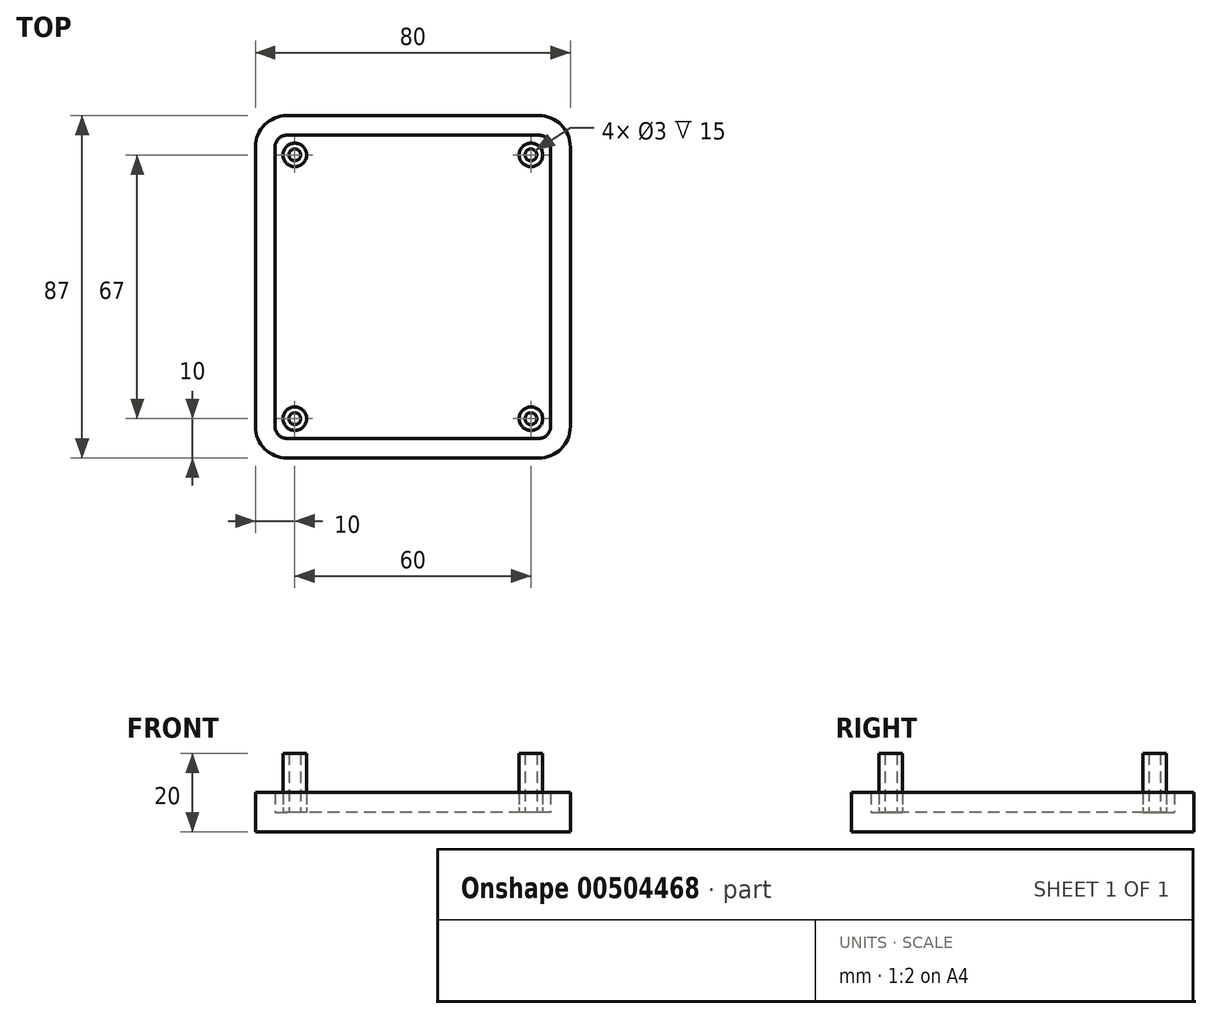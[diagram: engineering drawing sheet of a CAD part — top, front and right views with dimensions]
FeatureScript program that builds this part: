
annotation { "Feature Type Name" : "Feature", "Feature Type Description" : "" }
export const myFeature = defineFeature(function(context is Context, id is Id, definition is map)
    precondition{}
    {
        {
            var Q0;
            Q0=qCreatedBy(makeId("Top.planeOp"),FACE);
            var sketch = newSketch(context, id + "F0", { "sketchPlane" : qUnion([Q0])});
            skLineSegment(sketch, "E0.bottom", {"start": v(32, 38.5) * mm, "end": v(-32, 38.5) * mm});
            skLineSegment(sketch, "E0.top", {"start": v(32, -38.5) * mm, "end": v(-32, -38.5) * mm});
            skLineSegment(sketch, "E0.left", {"start": v(35, 35.5) * mm, "end": v(35, -35.5) * mm});
            skLineSegment(sketch, "E0.right", {"start": v(-35, 35.5) * mm, "end": v(-35, -35.5) * mm});
            skPoint(sketch, "E0.middle", {"position": v(0, 0) * mm});
            skPoint(sketch, "E1.visualSharp", {"position": v(-35, 38.5) * mm});
            skArc(sketch, "E1.filletArc", {"start": v(-32, 38.5) * mm, "mid": v(-34.12, 37.62) * mm, "end": v(-35, 35.5) * mm});
            skPoint(sketch, "E2.visualSharp", {"position": v(35, 38.5) * mm});
            skArc(sketch, "E2.filletArc", {"start": v(35, 35.5) * mm, "mid": v(34.12, 37.62) * mm, "end": v(32, 38.5) * mm});
            skPoint(sketch, "E3.visualSharp", {"position": v(35, -38.5) * mm});
            skArc(sketch, "E3.filletArc", {"start": v(32, -38.5) * mm, "mid": v(34.12, -37.62) * mm, "end": v(35, -35.5) * mm});
            skPoint(sketch, "E4.visualSharp", {"position": v(-35, -38.5) * mm});
            skArc(sketch, "E4.filletArc", {"start": v(-35, -35.5) * mm, "mid": v(-34.12, -37.62) * mm, "end": v(-32, -38.5) * mm});
            skLineSegment(sketch, "E5.bottom", {"start": v(32, 43.5) * mm, "end": v(-32, 43.5) * mm});
            skLineSegment(sketch, "E5.top", {"start": v(32, -43.5) * mm, "end": v(-32, -43.5) * mm});
            skLineSegment(sketch, "E5.left", {"start": v(40, 35.5) * mm, "end": v(40, -35.5) * mm});
            skLineSegment(sketch, "E5.right", {"start": v(-40, 35.5) * mm, "end": v(-40, -35.5) * mm});
            skPoint(sketch, "E6.visualSharp", {"position": v(-40, 43.5) * mm});
            skArc(sketch, "E6.filletArc", {"start": v(-32, 43.5) * mm, "mid": v(-37.66, 41.16) * mm, "end": v(-40, 35.5) * mm});
            skPoint(sketch, "E7.visualSharp", {"position": v(40, 43.5) * mm});
            skArc(sketch, "E7.filletArc", {"start": v(40, 35.5) * mm, "mid": v(37.66, 41.16) * mm, "end": v(32, 43.5) * mm});
            skPoint(sketch, "E8.visualSharp", {"position": v(40, -43.5) * mm});
            skArc(sketch, "E8.filletArc", {"start": v(32, -43.5) * mm, "mid": v(37.66, -41.16) * mm, "end": v(40, -35.5) * mm});
            skPoint(sketch, "E9.visualSharp", {"position": v(-40, -43.5) * mm});
            skArc(sketch, "E9.filletArc", {"start": v(-40, -35.5) * mm, "mid": v(-37.66, -41.16) * mm, "end": v(-32, -43.5) * mm});
            skCircle(sketch, "E10", {"center": v(30, 33.5) * mm, "radius": 2 * mm, "construction": true});
            skCircle(sketch, "E11", {"center": v(-30, 33.5) * mm, "radius": 2 * mm, "construction": true});
            skCircle(sketch, "E12", {"center": v(-30, -33.5) * mm, "radius": 2 * mm, "construction": true});
            skCircle(sketch, "E13", {"center": v(30, -33.5) * mm, "radius": 2 * mm, "construction": true});
            skCircle(sketch, "E14", {"center": v(-30, 33.5) * mm, "radius": 1.5 * mm});
            skCircle(sketch, "E15", {"center": v(-30, 33.5) * mm, "radius": 3 * mm});
            skCircle(sketch, "E16", {"center": v(30, 33.5) * mm, "radius": 1.5 * mm});
            skCircle(sketch, "E17", {"center": v(30, 33.5) * mm, "radius": 3 * mm});
            skCircle(sketch, "E18", {"center": v(30, -33.5) * mm, "radius": 1.5 * mm});
            skCircle(sketch, "E19", {"center": v(30, -33.5) * mm, "radius": 3 * mm});
            skCircle(sketch, "E20", {"center": v(-30, -33.5) * mm, "radius": 1.5 * mm});
            skCircle(sketch, "E21", {"center": v(-30, -33.5) * mm, "radius": 3 * mm});
            skSolve(sketch);
        }
        {
            var Q0;
            Q0=makeQuery(id+"F0.imprint","IMPRINT",FACE,{"disambiguationData":[TD([[makeQuery(id+"F0.imprint","IMPRINT",EDGE,{"derivedFrom":sQuery(id+"F0.wireOp",EDGE,"E0.bottom")}),-1.0]])]});
            extrude(context, id + "F1", {"entities" : qUnion([Q0]), "depth" : 10 * mm});
        }
        {
            var Q0;
            Q0=makeQuery(id+"F0.imprint","IMPRINT",FACE,{"disambiguationData":[TD([[makeQuery(id+"F0.imprint","IMPRINT",EDGE,{"derivedFrom":sQuery(id+"F0.wireOp",EDGE,"E0.bottom")}),1.0]])]});
            var Q1;
            Q1=makeQuery(id+"F0.imprint","IMPRINT",FACE,{"disambiguationData":[TD([[makeQuery(id+"F0.imprint","IMPRINT",EDGE,{"derivedFrom":sQuery(id+"F0.wireOp",EDGE,"E20")}),1.0]])]});
            var Q2;
            Q2=makeQuery(id+"F0.imprint","IMPRINT",FACE,{"disambiguationData":[TD([[makeQuery(id+"F0.imprint","IMPRINT",EDGE,{"derivedFrom":sQuery(id+"F0.wireOp",EDGE,"E18")}),1.0]])]});
            var Q3;
            Q3=makeQuery(id+"F0.imprint","IMPRINT",FACE,{"disambiguationData":[TD([[makeQuery(id+"F0.imprint","IMPRINT",EDGE,{"derivedFrom":sQuery(id+"F0.wireOp",EDGE,"E16")}),1.0]])]});
            var Q4;
            Q4=makeQuery(id+"F0.imprint","IMPRINT",FACE,{"disambiguationData":[TD([[makeQuery(id+"F0.imprint","IMPRINT",EDGE,{"derivedFrom":sQuery(id+"F0.wireOp",EDGE,"E14")}),1.0]])]});
            extrude(context, id + "F2", {"entities" : qUnion([Q0, Q1, Q2, Q3, Q4]), "operationType" : NewBodyOperationType.ADD, "depth" : 5 * mm});
        }
        {
            var Q0;
            Q0=makeQuery(id+"F0.imprint","IMPRINT",FACE,{"disambiguationData":[TD([[makeQuery(id+"F0.imprint","IMPRINT",EDGE,{"derivedFrom":sQuery(id+"F0.wireOp",EDGE,"E14")}),-1.0]])]});
            var Q1;
            Q1=makeQuery(id+"F0.imprint","IMPRINT",FACE,{"disambiguationData":[TD([[makeQuery(id+"F0.imprint","IMPRINT",EDGE,{"derivedFrom":sQuery(id+"F0.wireOp",EDGE,"E16")}),-1.0]])]});
            var Q2;
            Q2=makeQuery(id+"F0.imprint","IMPRINT",FACE,{"disambiguationData":[TD([[makeQuery(id+"F0.imprint","IMPRINT",EDGE,{"derivedFrom":sQuery(id+"F0.wireOp",EDGE,"E18")}),-1.0]])]});
            var Q3;
            Q3=makeQuery(id+"F0.imprint","IMPRINT",FACE,{"disambiguationData":[TD([[makeQuery(id+"F0.imprint","IMPRINT",EDGE,{"derivedFrom":sQuery(id+"F0.wireOp",EDGE,"E20")}),-1.0]])]});
            extrude(context, id + "F3", {"entities" : qUnion([Q0, Q1, Q2, Q3]), "operationType" : NewBodyOperationType.ADD, "depth" : 20 * mm});
        }
    });
